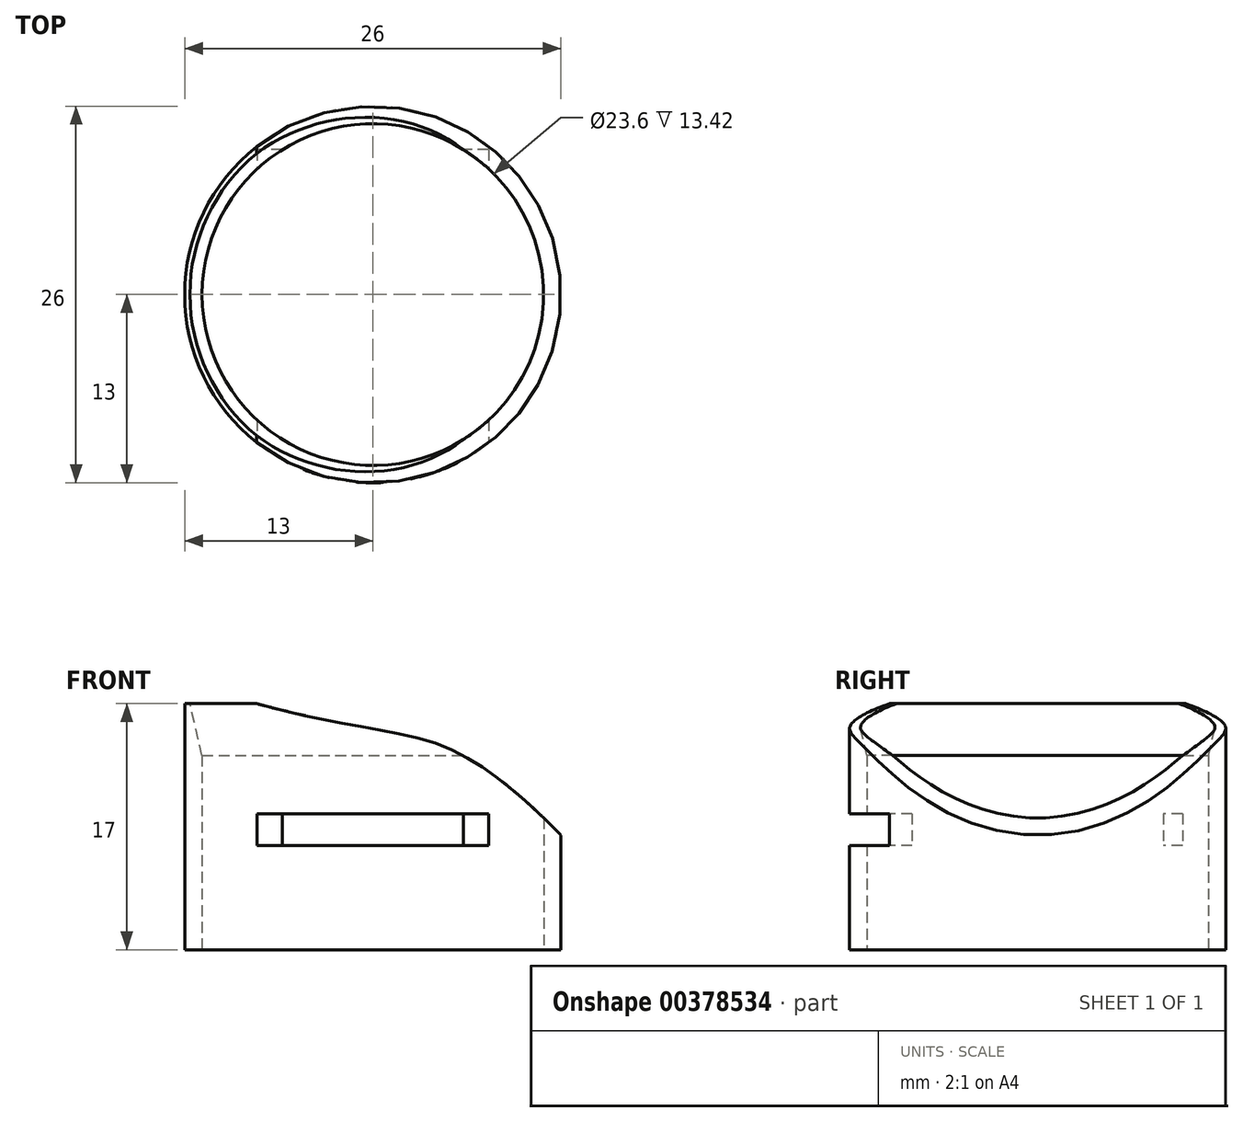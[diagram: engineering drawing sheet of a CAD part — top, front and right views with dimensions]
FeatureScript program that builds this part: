
annotation { "Feature Type Name" : "Feature", "Feature Type Description" : "" }
export const myFeature = defineFeature(function(context is Context, id is Id, definition is map)
    precondition{}
    {
        {
            var Q0;
            Q0=qCreatedBy(makeId("Front.planeOp"),FACE);
            var sketch = newSketch(context, id + "F0", { "sketchPlane" : qUnion([Q0])});
            skLineSegment(sketch, "E0.bottom", {"start": v(0, 0) * mm, "end": v(-11.8, 0) * mm});
            skLineSegment(sketch, "E0.top", {"start": v(0, 17) * mm, "end": v(-11.8, 17) * mm});
            skLineSegment(sketch, "E0.left", {"start": v(0, 0) * mm, "end": v(0, 17) * mm});
            skLineSegment(sketch, "E0.right", {"start": v(-11.8, 0) * mm, "end": v(-11.8, 17) * mm});
            skLineSegment(sketch, "E1.bottom", {"start": v(0, 0) * mm, "end": v(-13, 0) * mm});
            skLineSegment(sketch, "E1.top", {"start": v(0, 17) * mm, "end": v(-13, 17) * mm});
            skLineSegment(sketch, "E1.right", {"start": v(-13, 0) * mm, "end": v(-13, 17) * mm});
            skLineSegment(sketch, "E2", {"start": v(-12.63, 17) * mm, "end": v(-11.8, 13.42) * mm});
            skLineSegment(sketch, "E3.bottom", {"start": v(-11.8, 7.1) * mm, "end": v(-9.8, 7.1) * mm});
            skLineSegment(sketch, "E3.top", {"start": v(-11.8, 9.6) * mm, "end": v(-9.8, 9.6) * mm});
            skLineSegment(sketch, "E3.left", {"start": v(-11.8, 7.1) * mm, "end": v(-11.8, 9.6) * mm});
            skLineSegment(sketch, "E3.right", {"start": v(-9.8, 7.1) * mm, "end": v(-9.8, 9.6) * mm});
            skLineSegment(sketch, "E4", {"start": v(-11.8, 13.42) * mm, "end": v(-9.58, 3.89) * mm});
            skSolve(sketch);
        }
        {
            var Q0;
            {var subQ0=sQuery(id+"F0.wireOp",EDGE,"E1.right");Q0=makeQuery(id+"F0.imprint","IMPRINT",FACE,{"disambiguationData":[TD([[makeQuery(id+"F0.imprint","IMPRINT",EDGE,{"derivedFrom":subQ0}),-1.0]])]});}
            var Q1;
            {var subQ0=sQuery(id+"F0.wireOp",EDGE,"E3.left");Q1=makeQuery(id+"F0.imprint","IMPRINT",FACE,{"disambiguationData":[TD([[makeQuery(id+"F0.imprint","IMPRINT",EDGE,{"derivedFrom":subQ0}),-1.0]])]});}
            var Q2;
            Q2=sQuery(id+"F0.wireOp",EDGE,"E0.left");
            revolve(context, id + "F1", {"entities" : qUnion([Q0, Q1]), "axis" : qUnion([Q2]), "revolveType" : RevolveType.FULL});
        }
        {
            var Q0;
            Q0=qCreatedBy(makeId("Front.planeOp"),FACE);
            cPlane(context, id + "F2", {"entities" : qUnion([Q0]), "cplaneType" : CPlaneType.OFFSET, "offset" : 13 * mm, "width" : 150 * mm, "height" : 150 * mm});
        }
        {
            var Q0;
            Q0=qCreatedBy(id+"F2.planeOp",FACE);
            var sketch = newSketch(context, id + "F3", { "sketchPlane" : qUnion([Q0])});
            skLineSegment(sketch, "E5.bottom", {"start": v(8, 7.2) * mm, "end": v(-8, 7.2) * mm});
            skLineSegment(sketch, "E5.top", {"start": v(8, 9.4) * mm, "end": v(-8, 9.4) * mm});
            skLineSegment(sketch, "E5.left", {"start": v(8, 7.2) * mm, "end": v(8, 9.4) * mm});
            skLineSegment(sketch, "E5.right", {"start": v(-8, 7.2) * mm, "end": v(-8, 9.4) * mm});
            skPoint(sketch, "E5.middle", {"position": v(0, 8.3) * mm});
            skFitSpline(sketch, "E6", {"points": [v(-9.9, 17.52) * mm, v(5.72, 13.68) * mm, v(17.09, 3.41) * mm], "startDerivative": vector(52.43, -15.38) * mm, "endDerivative": vector(24.89, -28.94) * mm});
            skFitSpline(sketch, "E7", {"points": [v(-9.9, 17.52) * mm, v(-10.3, 19.67) * mm, v(-3.97, 21.35) * mm, v(14.54, 20.23) * mm, v(22.24, 13.25) * mm, v(20.72, 6.91) * mm, v(20.44, 6.41) * mm, v(17.09, 3.41) * mm], "startDerivative": vector(-12.35, 27.08) * mm, "endDerivative": vector(-35.2, -30.33) * mm});
            skSolve(sketch);
        }
        {
            var Q0;
            Q0=makeQuery(id+"F3.imprint","IMPRINT",FACE,{"disambiguationData":[TD([[makeQuery(id+"F3.imprint","IMPRINT",EDGE,{"derivedFrom":sQuery(id+"F3.wireOp",EDGE,"E6")}),1.0]])]});
            extrude(context, id + "F4", {"entities" : qUnion([Q0]), "operationType" : NewBodyOperationType.REMOVE, "endBound" : BoundingType.THROUGH_ALL, "oppositeDirection" : true, "depth" : 25 * mm});
        }
        {
            var Q0;
            Q0=makeQuery(id+"F3.imprint","IMPRINT",FACE,{"disambiguationData":[TD([[makeQuery(id+"F3.imprint","IMPRINT",EDGE,{"derivedFrom":sQuery(id+"F3.wireOp",EDGE,"E5.bottom")}),-1.0]])]});
            extrude(context, id + "F5", {"entities" : qUnion([Q0]), "operationType" : NewBodyOperationType.REMOVE, "oppositeDirection" : true, "depth" : 23 * mm});
        }
    });
